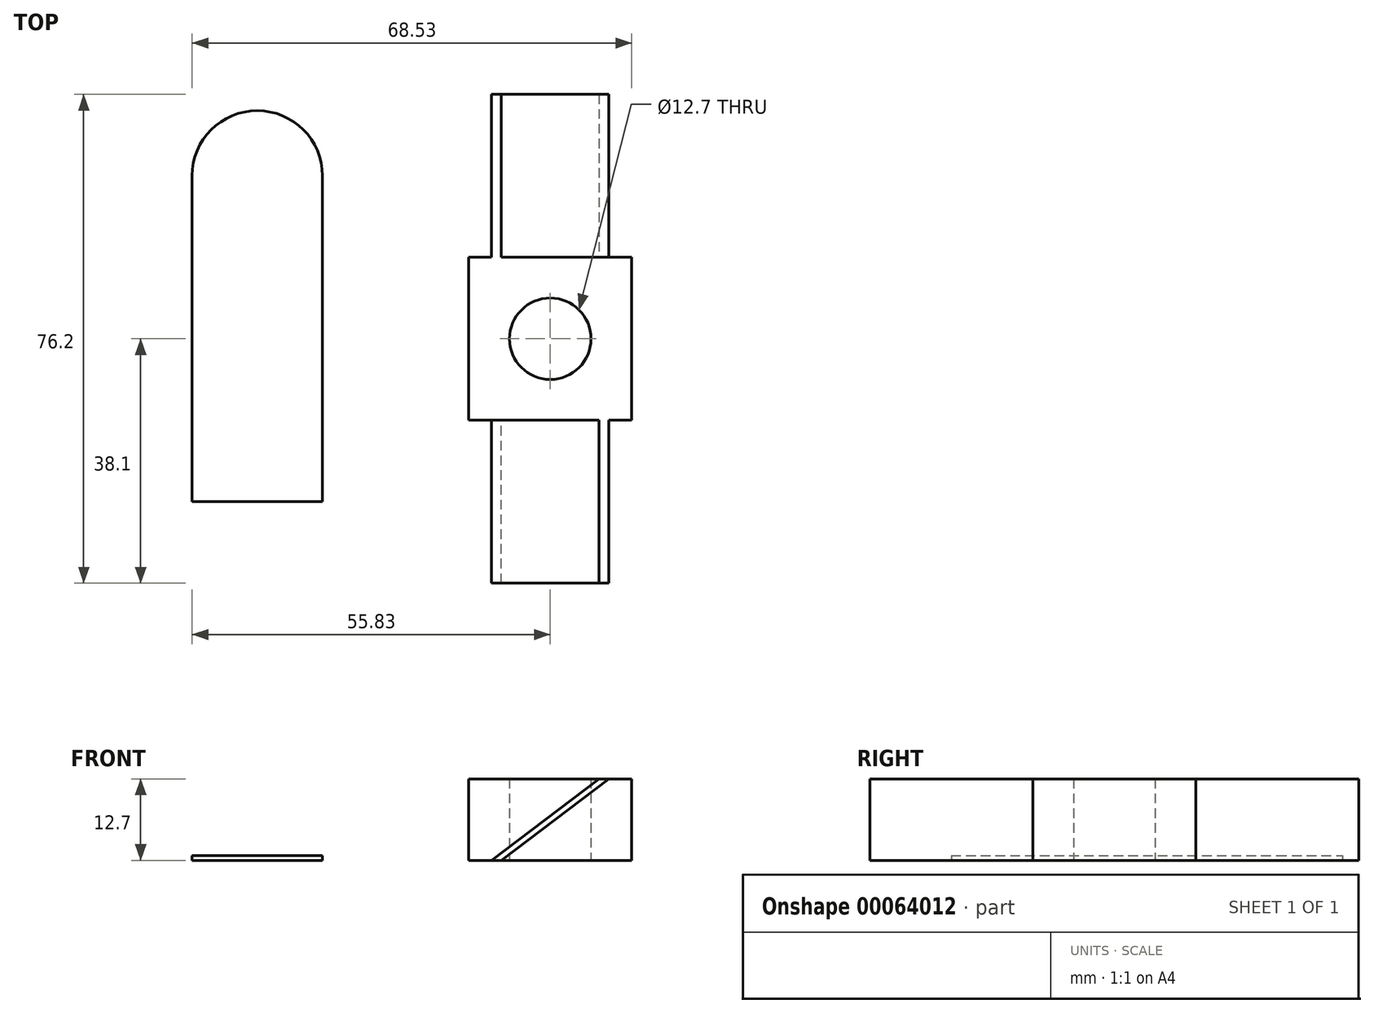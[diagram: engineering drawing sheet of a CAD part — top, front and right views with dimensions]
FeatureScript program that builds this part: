
annotation { "Feature Type Name" : "Feature", "Feature Type Description" : "" }
export const myFeature = defineFeature(function(context is Context, id is Id, definition is map)
    precondition{}
    {
        {
            var Q0;
            Q0=qCreatedBy(makeId("Top.planeOp"),FACE);
            var sketch = newSketch(context, id + "F0", { "sketchPlane" : qUnion([Q0])});
            skCircle(sketch, "E0", {"center": v(0, 0) * mm, "radius": 6.35 * mm});
            skLineSegment(sketch, "E1.rect.bottom", {"start": v(-12.7, -12.7) * mm, "end": v(12.7, -12.7) * mm});
            skLineSegment(sketch, "E1.rect.top", {"start": v(-12.7, 12.7) * mm, "end": v(12.7, 12.7) * mm});
            skLineSegment(sketch, "E1.rect.left", {"start": v(-12.7, -12.7) * mm, "end": v(-12.7, 12.7) * mm});
            skLineSegment(sketch, "E1.rect.right", {"start": v(12.7, -12.7) * mm, "end": v(12.7, 12.7) * mm});
            skSolve(sketch);
        }
        {
            var Q0;
            Q0 = qSketchRegion(id + "F0", true);
            extrude(context, id + "F1", {"entities" : qUnion([Q0]), "depth" : 12.7 * mm});
        }
        {
            var Q0;
            Q0=makeQuery(id+"F1.opExtrude","SWEPT_FACE",FACE,{"disambiguationData":[OSD([sQuery(id+"F0.wireOp",EDGE,"E1.rect.top")])]});
            var sketch = newSketch(context, id + "F2", { "sketchPlane" : qUnion([Q0])});
            skLineSegment(sketch, "E2", {"start": v(0, 12.7) * mm, "end": v(0, 0) * mm});
            skPoint(sketch, "E3", {"position": v(-7.62, 12.7) * mm});
            skLineSegment(sketch, "E4", {"start": v(-7.62, 12.7) * mm, "end": v(-5.64, 12.7) * mm});
            skPoint(sketch, "E5", {"position": v(-9.14, 12.7) * mm});
            skPoint(sketch, "E6", {"position": v(7.62, 0) * mm});
            skPoint(sketch, "E7", {"position": v(9.14, 0) * mm});
            skLineSegment(sketch, "E8.MirrorCS", {"start": v(-9.14, 0) * mm, "end": v(7.62, 12.7) * mm});
            skLineSegment(sketch, "E9.MirrorCS", {"start": v(9.14, 12.7) * mm, "end": v(-7.62, 0) * mm});
            skLineSegment(sketch, "E10.MirrorCS", {"start": v(9.14, 12.7) * mm, "end": v(7.62, 12.7) * mm});
            skLineSegment(sketch, "E11.MirrorCS", {"start": v(-7.62, 0) * mm, "end": v(-9.14, 0) * mm});
            skSolve(sketch);
        }
        {
            var Q0;
            Q0 = qSketchRegion(id + "F2", true);
            extrude(context, id + "F3", {"entities" : qUnion([Q0]), "operationType" : NewBodyOperationType.ADD, "offsetDistance" : 25.4 * mm, "depth" : 25.4 * mm});
        }
        {
            var Q0;
            Q0=makeQuery(id+"F1.opExtrude","SWEPT_FACE",FACE,{"disambiguationData":[OSD([sQuery(id+"F0.wireOp",EDGE,"E1.rect.bottom")])]});
            var sketch = newSketch(context, id + "F4", { "sketchPlane" : qUnion([Q0])});
            skPoint(sketch, "E12", {"position": v(-7.62, 12.7) * mm});
            skPoint(sketch, "E13", {"position": v(-9.14, 12.7) * mm});
            skPoint(sketch, "E14", {"position": v(9.14, 0) * mm});
            skPoint(sketch, "E15", {"position": v(7.62, 0) * mm});
            skLineSegment(sketch, "E16", {"start": v(0, 12.7) * mm, "end": v(0, -0.35) * mm});
            skLineSegment(sketch, "E17.MirrorCS", {"start": v(7.62, 12.7) * mm, "end": v(-9.14, 0) * mm});
            skLineSegment(sketch, "E18.MirrorCS", {"start": v(9.14, 12.7) * mm, "end": v(-7.62, 0) * mm});
            skLineSegment(sketch, "E19", {"start": v(-9.14, 0) * mm, "end": v(-7.62, 0) * mm});
            skLineSegment(sketch, "E20", {"start": v(7.62, 12.7) * mm, "end": v(9.14, 12.7) * mm});
            skSolve(sketch);
        }
        {
            var Q0;
            Q0 = qSketchRegion(id + "F4", true);
            extrude(context, id + "F5", {"entities" : qUnion([Q0]), "operationType" : NewBodyOperationType.ADD, "offsetDistance" : 25.4 * mm, "depth" : 25.4 * mm});
        }
        {
            var Q0;
            Q0=qCreatedBy(makeId("Top.planeOp"),FACE);
            var sketch = newSketch(context, id + "F6", { "sketchPlane" : qUnion([Q0])});
            skLineSegment(sketch, "E21.rect.bottom", {"start": v(-55.83, -25.4) * mm, "end": v(-35.51, -25.4) * mm});
            skLineSegment(sketch, "E21.rect.left", {"start": v(-55.83, -25.4) * mm, "end": v(-55.83, 25.4) * mm});
            skLineSegment(sketch, "E21.rect.right", {"start": v(-35.51, -25.4) * mm, "end": v(-35.51, 25.4) * mm});
            skPoint(sketch, "E21.rect.middle", {"position": v(-45.67, 0) * mm});
            skArc(sketch, "E22", {"start": v(-35.51, 25.4) * mm, "mid": v(-45.67, 35.56) * mm, "end": v(-55.83, 25.4) * mm});
            skSolve(sketch);
        }
        {
            var Q0;
            Q0 = qSketchRegion(id + "F6", true);
            extrude(context, id + "F7", {"entities" : qUnion([Q0]), "depth" : 0.76 * mm});
        }
    });
